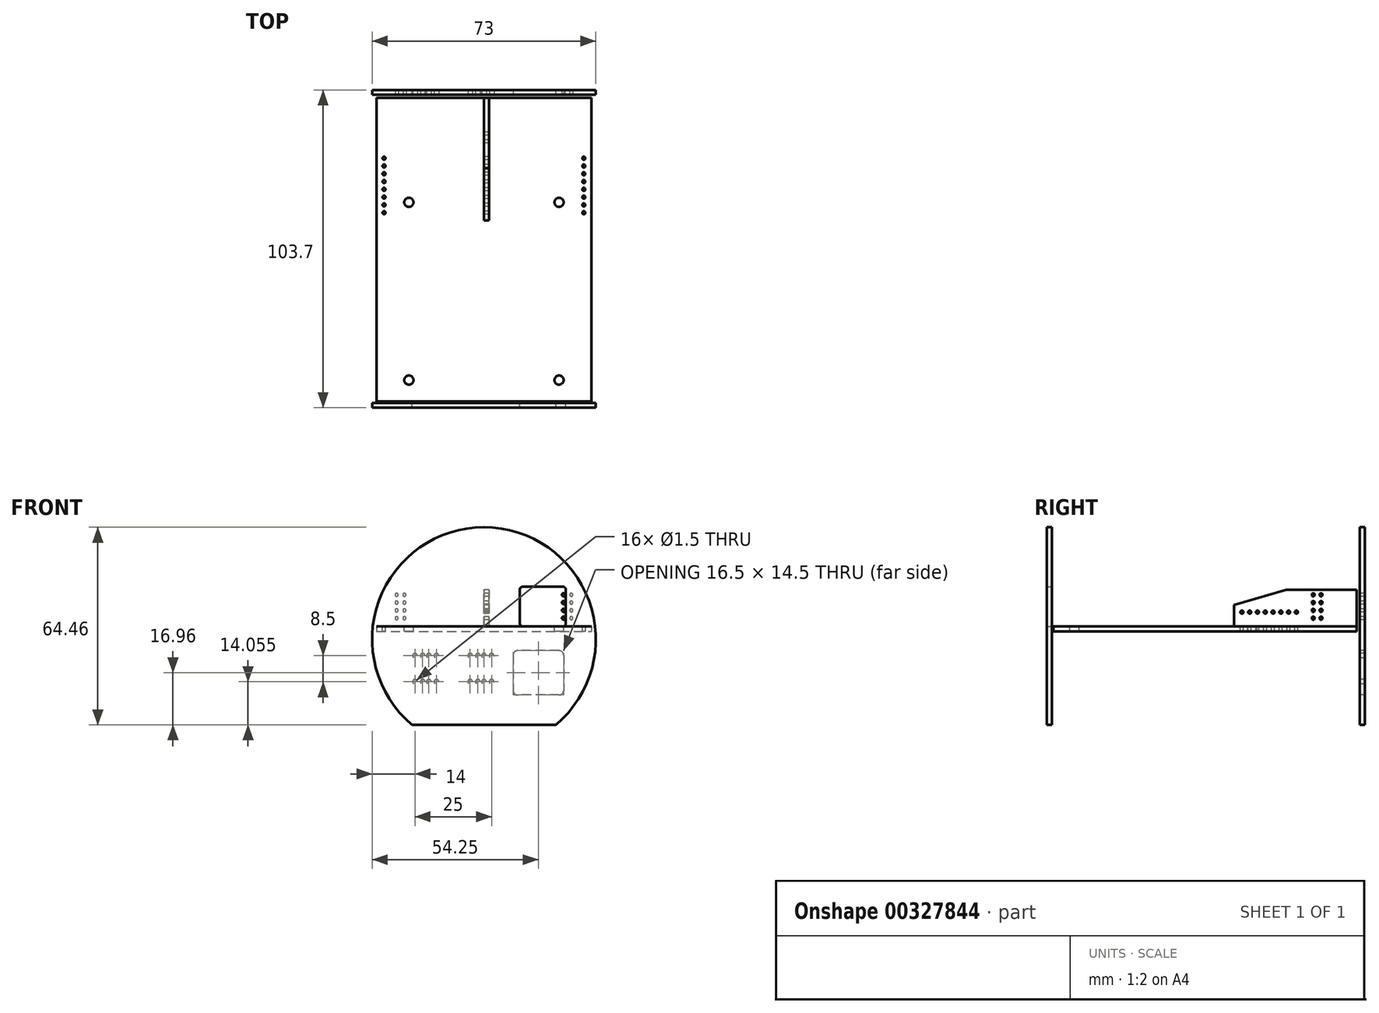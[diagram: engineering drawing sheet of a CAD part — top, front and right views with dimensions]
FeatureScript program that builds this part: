
annotation { "Feature Type Name" : "Feature", "Feature Type Description" : "" }
export const myFeature = defineFeature(function(context is Context, id is Id, definition is map)
    precondition{}
    {
        {
            var Q0;
            Q0=qCreatedBy(makeId("Front.planeOp"),FACE);
            var sketch = newSketch(context, id + "F0", { "sketchPlane" : qUnion([Q0])});
            skCircle(sketch, "E0", {"center": v(0, 0) * mm, "radius": 36.5 * mm});
            skLineSegment(sketch, "E1", {"start": v(-23.46, -27.96) * mm, "end": v(23.46, -27.96) * mm});
            skLineSegment(sketch, "E2", {"start": v(0, 0) * mm, "end": v(-23.46, -27.96) * mm, "construction": true});
            skLineSegment(sketch, "E3", {"start": v(0, 0) * mm, "end": v(23.46, -27.96) * mm, "construction": true});
            skSolve(sketch);
        }
        {
            var Q0;
            {var subQ0=sQuery(id+"F0.wireOp",EDGE,"E1");Q0=makeQuery(id+"F0.imprint","IMPRINT",FACE,{"disambiguationData":[TD([[makeQuery(id+"F0.imprint","IMPRINT",EDGE,{"derivedFrom":subQ0}),1.0]])]});}
            extrude(context, id + "F1", {"entities" : qUnion([Q0]), "depth" : 1.6 * mm});
        }
        {
            var Q0;
            Q0=makeQuery(id+"F1.opExtrude","CAP_FACE",FACE,{"disambiguationData":[OSD([sQuery(id+"F0.wireOp",EDGE,"E0"),sQuery(id+"F0.wireOp",EDGE,"E1")])],"isStart":false});
            var sketch = newSketch(context, id + "F2", { "sketchPlane" : qUnion([Q0])});
            skCircle(sketch, "E4", {"center": v(28.5, 14.46) * mm, "radius": 0.5 * mm});
            skCircle(sketch, "E5.0.1.0", {"center": v(28.5, 11.92) * mm, "radius": 0.5 * mm});
            skCircle(sketch, "E5.0.2.0", {"center": v(28.5, 9.38) * mm, "radius": 0.5 * mm});
            skCircle(sketch, "E5.0.3.0", {"center": v(28.5, 6.84) * mm, "radius": 0.5 * mm});
            skCircle(sketch, "E5.1.0.0", {"center": v(25.96, 14.46) * mm, "radius": 0.5 * mm});
            skCircle(sketch, "E5.1.1.0", {"center": v(25.96, 11.92) * mm, "radius": 0.5 * mm});
            skCircle(sketch, "E5.1.2.0", {"center": v(25.96, 9.38) * mm, "radius": 0.5 * mm});
            skCircle(sketch, "E5.1.3.0", {"center": v(25.96, 6.84) * mm, "radius": 0.5 * mm});
            skLineSegment(sketch, "E5.direction1", {"start": v(28.5, 14.46) * mm, "end": v(25.96, 14.46) * mm, "construction": true});
            skLineSegment(sketch, "E5.direction2", {"start": v(28.5, 14.46) * mm, "end": v(28.5, 11.92) * mm, "construction": true});
            skLineSegment(sketch, "E6.bottom", {"start": v(24.5, -3.75) * mm, "end": v(11, -3.75) * mm});
            skLineSegment(sketch, "E6.top", {"start": v(24.5, -18.25) * mm, "end": v(11, -18.25) * mm});
            skLineSegment(sketch, "E6.left", {"start": v(26, -5.25) * mm, "end": v(26, -16.75) * mm});
            skLineSegment(sketch, "E6.right", {"start": v(9.5, -5.25) * mm, "end": v(9.5, -16.75) * mm});
            skPoint(sketch, "E6.middle", {"position": v(17.75, -11) * mm});
            skPoint(sketch, "E7.visualSharp", {"position": v(9.5, -3.75) * mm});
            skArc(sketch, "E7.filletArc", {"start": v(11, -3.75) * mm, "mid": v(9.94, -4.19) * mm, "end": v(9.5, -5.25) * mm});
            skPoint(sketch, "E8.visualSharp", {"position": v(26, -3.75) * mm});
            skArc(sketch, "E8.filletArc", {"start": v(26, -5.25) * mm, "mid": v(25.56, -4.19) * mm, "end": v(24.5, -3.75) * mm});
            skPoint(sketch, "E9.visualSharp", {"position": v(26, -18.25) * mm});
            skArc(sketch, "E9.filletArc", {"start": v(24.5, -18.25) * mm, "mid": v(25.56, -17.81) * mm, "end": v(26, -16.75) * mm});
            skPoint(sketch, "E10.visualSharp", {"position": v(9.5, -18.25) * mm});
            skArc(sketch, "E10.filletArc", {"start": v(9.5, -16.75) * mm, "mid": v(9.94, -17.81) * mm, "end": v(11, -18.25) * mm});
            skCircle(sketch, "E11", {"center": v(-22.5, -5.4) * mm, "radius": 0.75 * mm});
            skCircle(sketch, "E12", {"center": v(-20, -5.4) * mm, "radius": 0.75 * mm});
            skCircle(sketch, "E13", {"center": v(-18, -5.4) * mm, "radius": 0.75 * mm});
            skCircle(sketch, "E14", {"center": v(-15.5, -5.4) * mm, "radius": 0.75 * mm});
            skCircle(sketch, "E15.0.1.0", {"center": v(-22.5, -13.9) * mm, "radius": 0.75 * mm});
            skCircle(sketch, "E15.0.1.1", {"center": v(-20, -13.9) * mm, "radius": 0.75 * mm});
            skCircle(sketch, "E15.0.1.2", {"center": v(-18, -13.9) * mm, "radius": 0.75 * mm});
            skCircle(sketch, "E15.0.1.3", {"center": v(-15.5, -13.9) * mm, "radius": 0.75 * mm});
            skCircle(sketch, "E15.1.0.0", {"center": v(-4.5, -5.4) * mm, "radius": 0.75 * mm});
            skCircle(sketch, "E15.1.0.1", {"center": v(-2, -5.4) * mm, "radius": 0.75 * mm});
            skCircle(sketch, "E15.1.0.2", {"center": v(0, -5.4) * mm, "radius": 0.75 * mm});
            skCircle(sketch, "E15.1.0.3", {"center": v(2.5, -5.4) * mm, "radius": 0.75 * mm});
            skCircle(sketch, "E15.1.1.0", {"center": v(-4.5, -13.9) * mm, "radius": 0.75 * mm});
            skCircle(sketch, "E15.1.1.1", {"center": v(-2, -13.9) * mm, "radius": 0.75 * mm});
            skCircle(sketch, "E15.1.1.2", {"center": v(0, -13.9) * mm, "radius": 0.75 * mm});
            skCircle(sketch, "E15.1.1.3", {"center": v(2.5, -13.9) * mm, "radius": 0.75 * mm});
            skLineSegment(sketch, "E15.direction1", {"start": v(-22.5, -5.4) * mm, "end": v(-4.5, -5.4) * mm, "construction": true});
            skLineSegment(sketch, "E15.direction2", {"start": v(-22.5, -5.4) * mm, "end": v(-22.5, -13.9) * mm, "construction": true});
            skPoint(sketch, "E16", {"position": v(-36.5, 0) * mm});
            skLineSegment(sketch, "E17", {"start": v(0, 0) * mm, "end": v(0, 16.77) * mm, "construction": true});
            skCircle(sketch, "E18.MirrorC", {"center": v(-25.96, 6.84) * mm, "radius": 0.5 * mm});
            skCircle(sketch, "E19.MirrorC", {"center": v(-25.96, 9.38) * mm, "radius": 0.5 * mm});
            skCircle(sketch, "E20.MirrorC", {"center": v(-25.96, 11.92) * mm, "radius": 0.5 * mm});
            skCircle(sketch, "E21.MirrorC", {"center": v(-25.96, 14.46) * mm, "radius": 0.5 * mm});
            skCircle(sketch, "E22.MirrorC", {"center": v(-28.5, 14.46) * mm, "radius": 0.5 * mm});
            skCircle(sketch, "E23.MirrorC", {"center": v(-28.5, 11.92) * mm, "radius": 0.5 * mm});
            skCircle(sketch, "E24.MirrorC", {"center": v(-28.5, 9.38) * mm, "radius": 0.5 * mm});
            skCircle(sketch, "E25.MirrorC", {"center": v(-28.5, 6.84) * mm, "radius": 0.5 * mm});
            skLineSegment(sketch, "E26", {"start": v(28.5, 6.84) * mm, "end": v(25.96, 14.46) * mm, "construction": true});
            skLineSegment(sketch, "E27.bottom", {"start": v(29.73, 15.98) * mm, "end": v(24.73, 15.98) * mm, "construction": true});
            skLineSegment(sketch, "E27.top", {"start": v(29.73, 5.32) * mm, "end": v(24.73, 5.32) * mm, "construction": true});
            skLineSegment(sketch, "E27.left", {"start": v(29.73, 15.98) * mm, "end": v(29.73, 5.32) * mm, "construction": true});
            skLineSegment(sketch, "E27.right", {"start": v(24.73, 15.98) * mm, "end": v(24.73, 5.32) * mm, "construction": true});
            skPoint(sketch, "E27.middle", {"position": v(27.23, 10.65) * mm});
            skLineSegment(sketch, "E28", {"start": v(31.33, 17.45) * mm, "end": v(31.33, 3.87) * mm, "construction": true});
            skSolve(sketch);
        }
        {
            var Q0;
            Q0=qSketchRegion(id+"F2",true);
            extrude(context, id + "F3", {"entities" : qUnion([Q0]), "operationType" : NewBodyOperationType.REMOVE, "oppositeDirection" : true, "depth" : 25 * mm});
        }
        {
            var Q0;
            Q0=makeQuery(id+"F1.opExtrude","CAP_FACE",FACE,{"disambiguationData":[OSD([sQuery(id+"F0.wireOp",EDGE,"E0"),sQuery(id+"F0.wireOp",EDGE,"E1")])],"isStart":false});
            cPlane(context, id + "F4", {"entities" : qUnion([Q0]), "cplaneType" : CPlaneType.OFFSET, "offset" : 1 * mm, "width" : 150 * mm, "height" : 150 * mm});
        }
        {
            var Q0;
            Q0=qCreatedBy(id+"F4.planeOp",FACE);
            var sketch = newSketch(context, id + "F5", { "sketchPlane" : qUnion([Q0])});
            skLineSegment(sketch, "E29.bottom", {"start": v(-35, 4.12) * mm, "end": v(35, 4.12) * mm});
            skLineSegment(sketch, "E29.top", {"start": v(-35, 2.52) * mm, "end": v(35, 2.52) * mm});
            skLineSegment(sketch, "E29.left", {"start": v(-35, 4.12) * mm, "end": v(-35, 2.52) * mm});
            skLineSegment(sketch, "E29.right", {"start": v(35, 4.12) * mm, "end": v(35, 2.52) * mm});
            skPoint(sketch, "E29.middle", {"position": v(0, 3.32) * mm});
            skSolve(sketch);
        }
        {
            var Q0;
            Q0=qSketchRegion(id+"F5",true);
            extrude(context, id + "F6", {"entities" : qUnion([Q0]), "depth" : 99 * mm});
        }
        {
            var Q0;
            Q0=makeQuery(id+"F6.opExtrude","SWEPT_FACE",FACE,{"disambiguationData":[OSD([sQuery(id+"F5.wireOp",EDGE,"E29.bottom")])]});
            var sketch = newSketch(context, id + "F7", { "sketchPlane" : qUnion([Q0])});
            skCircle(sketch, "E30", {"center": v(-24.5, -36.67) * mm, "radius": 1.5 * mm});
            skCircle(sketch, "E31", {"center": v(24.5, -94.67) * mm, "radius": 1.5 * mm});
            skCircle(sketch, "E32", {"center": v(-24.5, -94.67) * mm, "radius": 1.5 * mm});
            skCircle(sketch, "E33", {"center": v(24.5, -36.67) * mm, "radius": 1.5 * mm});
            skCircle(sketch, "E34", {"center": v(-32.58, -22.28) * mm, "radius": 0.5 * mm});
            skCircle(sketch, "E35.0.1.0", {"center": v(-32.58, -24.82) * mm, "radius": 0.5 * mm});
            skCircle(sketch, "E35.0.2.0", {"center": v(-32.58, -27.36) * mm, "radius": 0.5 * mm});
            skCircle(sketch, "E35.0.3.0", {"center": v(-32.58, -29.9) * mm, "radius": 0.5 * mm});
            skCircle(sketch, "E35.0.4.0", {"center": v(-32.58, -32.44) * mm, "radius": 0.5 * mm});
            skCircle(sketch, "E35.0.5.0", {"center": v(-32.58, -34.98) * mm, "radius": 0.5 * mm});
            skCircle(sketch, "E35.0.6.0", {"center": v(-32.58, -37.52) * mm, "radius": 0.5 * mm});
            skCircle(sketch, "E35.0.7.0", {"center": v(-32.58, -40.06) * mm, "radius": 0.5 * mm});
            skLineSegment(sketch, "E35.direction1", {"start": v(-32.58, -22.28) * mm, "end": v(-4.7, -22.28) * mm, "construction": true});
            skLineSegment(sketch, "E35.direction2", {"start": v(-32.58, -22.28) * mm, "end": v(-32.58, -24.82) * mm, "construction": true});
            skLineSegment(sketch, "E36", {"start": v(0, 0) * mm, "end": v(0, -31.2) * mm, "construction": true});
            skPoint(sketch, "E36.endSnap0", {"position": v(0, -2.6) * mm});
            skCircle(sketch, "E37.MirrorC", {"center": v(32.58, -40.06) * mm, "radius": 0.5 * mm});
            skCircle(sketch, "E38.MirrorC", {"center": v(32.58, -37.52) * mm, "radius": 0.5 * mm});
            skCircle(sketch, "E39.MirrorC", {"center": v(32.58, -34.98) * mm, "radius": 0.5 * mm});
            skCircle(sketch, "E40.MirrorC", {"center": v(32.58, -32.44) * mm, "radius": 0.5 * mm});
            skCircle(sketch, "E41.MirrorC", {"center": v(32.58, -29.9) * mm, "radius": 0.5 * mm});
            skCircle(sketch, "E42.MirrorC", {"center": v(32.58, -27.36) * mm, "radius": 0.5 * mm});
            skCircle(sketch, "E43.MirrorC", {"center": v(32.58, -24.82) * mm, "radius": 0.5 * mm});
            skCircle(sketch, "E44.MirrorC", {"center": v(32.58, -22.28) * mm, "radius": 0.5 * mm});
            skSolve(sketch);
        }
        {
            var Q0;
            Q0=qSketchRegion(id+"F7",true);
            extrude(context, id + "F8", {"entities" : qUnion([Q0]), "operationType" : NewBodyOperationType.REMOVE, "oppositeDirection" : true, "depth" : 25 * mm});
        }
        {
            var Q0;
            Q0=qCreatedBy(makeId("Right.planeOp"),FACE);
            var sketch = newSketch(context, id + "F9", { "sketchPlane" : qUnion([Q0])});
            skLineSegment(sketch, "E45", {"start": v(-2.6, 16.12) * mm, "end": v(-2.6, 4.12) * mm});
            skLineSegment(sketch, "E46", {"start": v(-2.6, 4.12) * mm, "end": v(-42.6, 4.12) * mm});
            skLineSegment(sketch, "E47", {"start": v(-42.6, 4.12) * mm, "end": v(-42.6, 11.12) * mm});
            skLineSegment(sketch, "E48", {"start": v(-42.6, 11.12) * mm, "end": v(-25.6, 16.12) * mm});
            skLineSegment(sketch, "E49", {"start": v(-25.6, 16.12) * mm, "end": v(-2.6, 16.12) * mm});
            skCircle(sketch, "E50", {"center": v(-14.24, 14.46) * mm, "radius": 0.5 * mm});
            skCircle(sketch, "E51.0.1.0", {"center": v(-14.24, 11.92) * mm, "radius": 0.5 * mm});
            skCircle(sketch, "E51.0.2.0", {"center": v(-14.24, 9.38) * mm, "radius": 0.5 * mm});
            skCircle(sketch, "E51.0.3.0", {"center": v(-14.24, 6.84) * mm, "radius": 0.5 * mm});
            skCircle(sketch, "E51.1.0.0", {"center": v(-16.78, 14.46) * mm, "radius": 0.5 * mm});
            skCircle(sketch, "E51.1.1.0", {"center": v(-16.78, 11.92) * mm, "radius": 0.5 * mm});
            skCircle(sketch, "E51.1.2.0", {"center": v(-16.78, 9.38) * mm, "radius": 0.5 * mm});
            skCircle(sketch, "E51.1.3.0", {"center": v(-16.78, 6.84) * mm, "radius": 0.5 * mm});
            skLineSegment(sketch, "E51.direction1", {"start": v(-14.24, 14.46) * mm, "end": v(-16.78, 14.46) * mm, "construction": true});
            skLineSegment(sketch, "E51.direction2", {"start": v(-14.24, 14.46) * mm, "end": v(-14.24, 11.92) * mm, "construction": true});
            skCircle(sketch, "E52", {"center": v(-22.28, 8.8) * mm, "radius": 0.5 * mm});
            skCircle(sketch, "E53.1.0.0", {"center": v(-24.82, 8.8) * mm, "radius": 0.5 * mm});
            skCircle(sketch, "E53.2.0.0", {"center": v(-27.36, 8.8) * mm, "radius": 0.5 * mm});
            skCircle(sketch, "E53.3.0.0", {"center": v(-29.9, 8.8) * mm, "radius": 0.5 * mm});
            skLineSegment(sketch, "E53.direction1", {"start": v(-22.28, 8.8) * mm, "end": v(-24.82, 8.8) * mm, "construction": true});
            skLineSegment(sketch, "E53.direction2", {"start": v(-22.28, 8.8) * mm, "end": v(-22.28, 6.26) * mm, "construction": true});
            skLineSegment(sketch, "E54.0", {"start": v(-1.6, 14.97) * mm, "end": v(-1.6, 13.95) * mm, "construction": true});
            skPoint(sketch, "E55", {"position": v(-1.6, 14.46) * mm});
            skCircle(sketch, "E56.0.4.0", {"center": v(-32.44, 8.8) * mm, "radius": 0.5 * mm});
            skCircle(sketch, "E56.0.5.0", {"center": v(-34.98, 8.8) * mm, "radius": 0.5 * mm});
            skCircle(sketch, "E56.0.6.0", {"center": v(-37.52, 8.8) * mm, "radius": 0.5 * mm});
            skCircle(sketch, "E56.0.7.0", {"center": v(-40.06, 8.8) * mm, "radius": 0.5 * mm});
            skSolve(sketch);
        }
        {
            var Q0;
            Q0=qSketchRegion(id+"F9",true);
            extrude(context, id + "F10", {"entities" : qUnion([Q0]), "depth" : 1.6 * mm});
        }
        {
            var Q0;
            Q0=makeQuery(id+"F6.opExtrude","CAP_FACE",FACE,{"disambiguationData":[OSD([sQuery(id+"F5.wireOp",EDGE,"E29.bottom"),sQuery(id+"F5.wireOp",EDGE,"E29.top"),sQuery(id+"F5.wireOp",EDGE,"E29.left"),sQuery(id+"F5.wireOp",EDGE,"E29.right")])],"isStart":false});
            cPlane(context, id + "F11", {"entities" : qUnion([Q0]), "cplaneType" : CPlaneType.OFFSET, "offset" : 0.5 * mm, "width" : 150 * mm, "height" : 150 * mm});
        }
        {
            var Q0;
            Q0=qCreatedBy(id+"F11.planeOp",FACE);
            var sketch = newSketch(context, id + "F12", { "sketchPlane" : qUnion([Q0])});
            skCircle(sketch, "E57", {"center": v(0, 0) * mm, "radius": 36.5 * mm});
            skLineSegment(sketch, "E58.bottom", {"start": v(25.7, 17.12) * mm, "end": v(12.7, 17.12) * mm});
            skLineSegment(sketch, "E58.top", {"start": v(25.7, 4.12) * mm, "end": v(12.7, 4.12) * mm});
            skLineSegment(sketch, "E58.left", {"start": v(26.7, 16.12) * mm, "end": v(26.7, 5.12) * mm});
            skLineSegment(sketch, "E58.right", {"start": v(11.7, 16.12) * mm, "end": v(11.7, 5.12) * mm});
            skPoint(sketch, "E58.middle", {"position": v(19.2, 10.62) * mm});
            skPoint(sketch, "E59.visualSharp", {"position": v(11.7, 17.12) * mm});
            skArc(sketch, "E59.filletArc", {"start": v(12.7, 17.12) * mm, "mid": v(12, 16.83) * mm, "end": v(11.7, 16.12) * mm});
            skPoint(sketch, "E60.visualSharp", {"position": v(11.7, 4.12) * mm});
            skArc(sketch, "E60.filletArc", {"start": v(11.7, 5.12) * mm, "mid": v(12, 4.41) * mm, "end": v(12.7, 4.12) * mm});
            skPoint(sketch, "E61.visualSharp", {"position": v(26.7, 4.12) * mm});
            skArc(sketch, "E61.filletArc", {"start": v(25.7, 4.12) * mm, "mid": v(26.4, 4.41) * mm, "end": v(26.7, 5.12) * mm});
            skPoint(sketch, "E62.visualSharp", {"position": v(26.7, 17.12) * mm});
            skArc(sketch, "E62.filletArc", {"start": v(26.7, 16.12) * mm, "mid": v(26.4, 16.83) * mm, "end": v(25.7, 17.12) * mm});
            skLineSegment(sketch, "E63", {"start": v(0, 0) * mm, "end": v(-23.46, -27.96) * mm, "construction": true});
            skLineSegment(sketch, "E64", {"start": v(0, 0) * mm, "end": v(23.46, -27.96) * mm, "construction": true});
            skLineSegment(sketch, "E65", {"start": v(-23.46, -27.96) * mm, "end": v(23.46, -27.96) * mm});
            skSolve(sketch);
        }
        {
            var Q0;
            Q0=makeQuery(id+"F12.imprint","IMPRINT",FACE,{"disambiguationData":[TD([[makeQuery(id+"F12.imprint","IMPRINT",EDGE,{"derivedFrom":sQuery(id+"F12.wireOp",EDGE,"E58.bottom")}),-1.0]])]});
            extrude(context, id + "F13", {"entities" : qUnion([Q0]), "depth" : 1.6 * mm});
        }
    });
